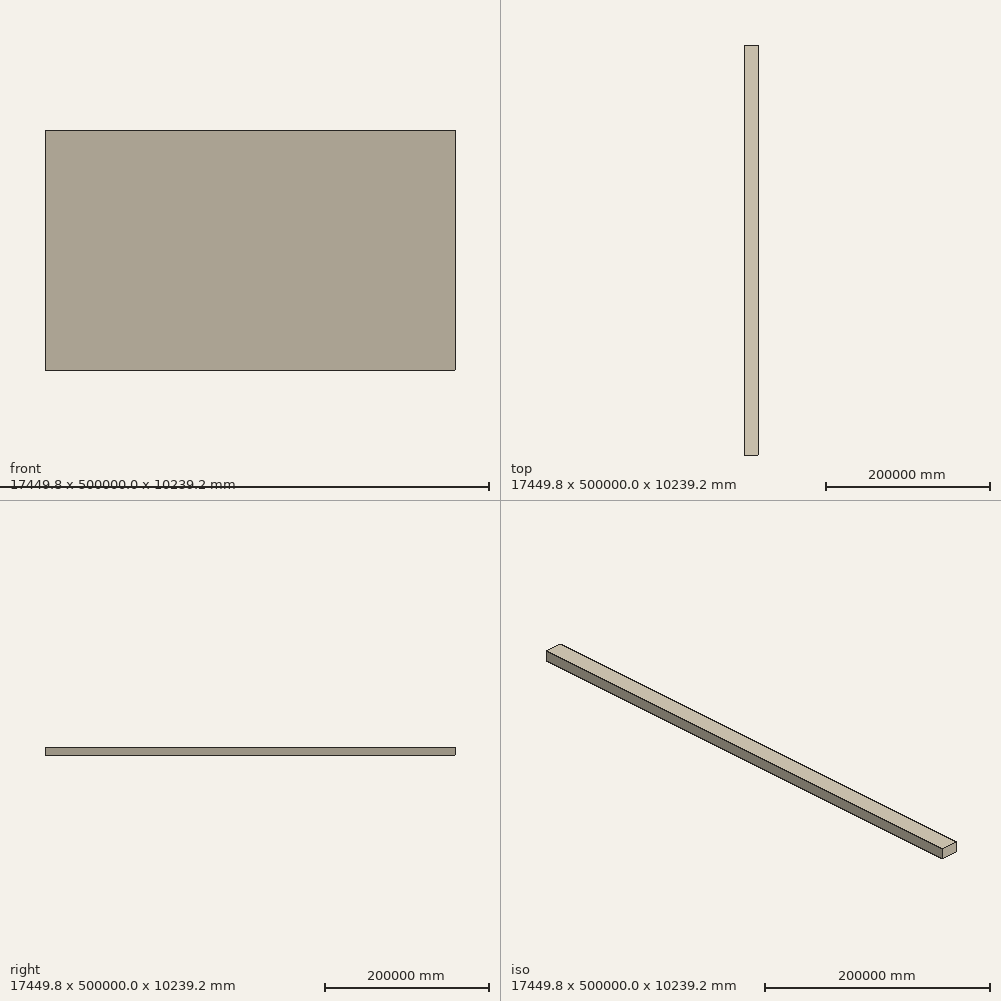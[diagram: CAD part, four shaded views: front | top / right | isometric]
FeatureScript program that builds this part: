
annotation { "Feature Type Name" : "Feature", "Feature Type Description" : "" }
export const myFeature = defineFeature(function(context is Context, id is Id, definition is map)
    precondition{}
    {
        {
            var Q0;
            Q0=qCreatedBy(makeId("Front.planeOp"),FACE);
            var sketch = newSketch(context, id + "F0", { "sketchPlane" : qUnion([Q0])});
            skLineSegment(sketch, "E0.bottom", {"start": v(-8721.62, 5125.37) * mm, "end": v(8728.18, 5125.37) * mm});
            skLineSegment(sketch, "E0.top", {"start": v(-8721.62, -5113.87) * mm, "end": v(8728.18, -5113.87) * mm});
            skLineSegment(sketch, "E0.left", {"start": v(-8721.62, 5125.37) * mm, "end": v(-8721.62, -5113.87) * mm});
            skLineSegment(sketch, "E0.right", {"start": v(8728.18, 5125.37) * mm, "end": v(8728.18, -5113.87) * mm});
            skSolve(sketch);
        }
        {
            var Q0;
            Q0 = qSketchRegion(id + "F0", true);
            extrude(context, id + "F1", {"entities" : qUnion([Q0]), "depth" : 500000 * mm});
        }
    });
